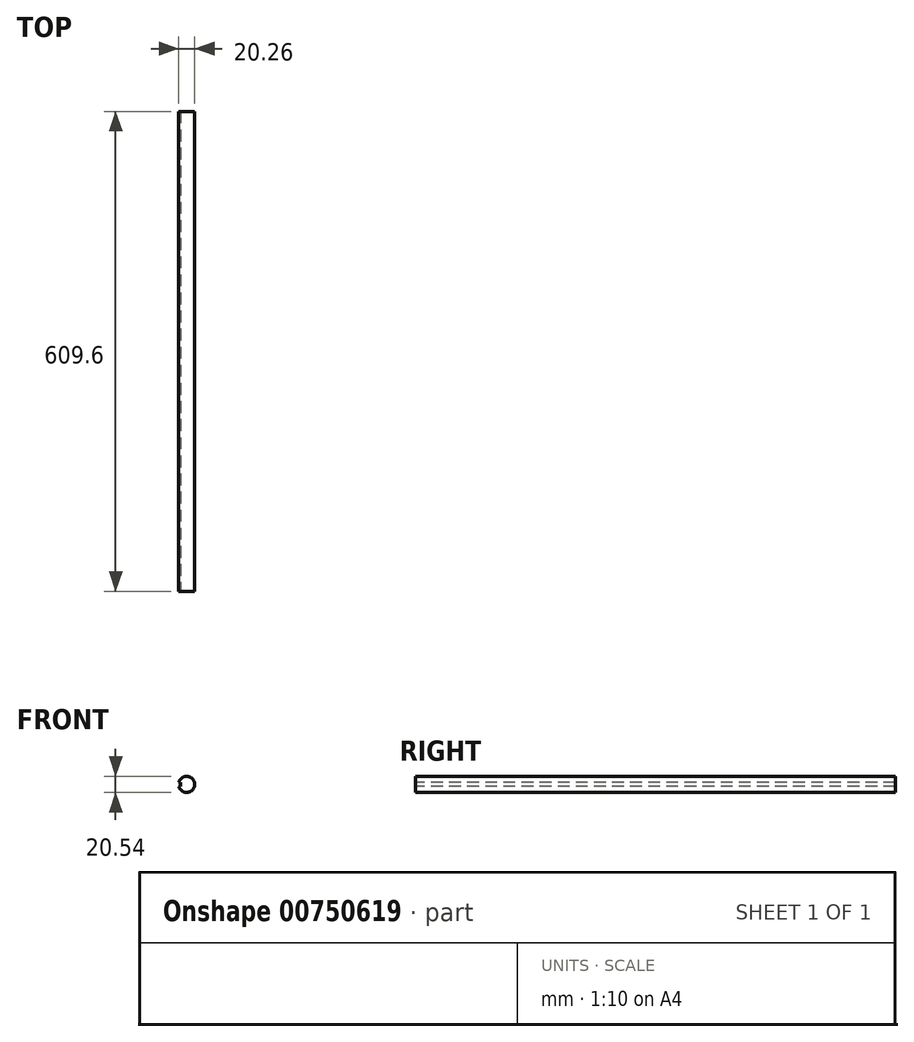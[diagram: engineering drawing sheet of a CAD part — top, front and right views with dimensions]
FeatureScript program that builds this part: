
annotation { "Feature Type Name" : "Feature", "Feature Type Description" : "" }
export const myFeature = defineFeature(function(context is Context, id is Id, definition is map)
    precondition{}
    {
        {
            var Q0;
            Q0=qCreatedBy(makeId("Front.planeOp"),FACE);
            var sketch = newSketch(context, id + "F0", { "sketchPlane" : qUnion([Q0])});
            skCircle(sketch, "E0", {"center": v(0, 0) * mm, "radius": 10.27 * mm});
            skLineSegment(sketch, "E1.bottom", {"start": v(-7.88, -2.39) * mm, "end": v(-12.66, -2.39) * mm});
            skLineSegment(sketch, "E1.top", {"start": v(-7.88, 2.39) * mm, "end": v(-12.66, 2.39) * mm});
            skLineSegment(sketch, "E1.left", {"start": v(-7.88, -2.39) * mm, "end": v(-7.88, 2.39) * mm});
            skLineSegment(sketch, "E1.right", {"start": v(-12.66, -2.39) * mm, "end": v(-12.66, 2.39) * mm});
            skPoint(sketch, "E1.middle", {"position": v(-10.27, 0) * mm});
            skSolve(sketch);
        }
        {
            var Q0;
            {var subQ5=sQuery(id+"F0.wireOp",EDGE,"E1.left");Q0=makeQuery(id+"F0.imprint","IMPRINT",FACE,{"disambiguationData":[TD([[makeQuery(id+"F0.imprint","IMPRINT",EDGE,{"derivedFrom":subQ5}),-1.0]])]});}
            extrude(context, id + "F1", {"entities" : qUnion([Q0]), "endBound" : BoundingType.SYMMETRIC, "oppositeDirection" : true, "depth" : 609.6 * mm, "offsetDistance" : 25.4 * mm});
        }
    });
